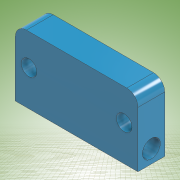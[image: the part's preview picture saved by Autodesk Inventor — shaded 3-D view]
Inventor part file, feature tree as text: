
AUTODESK INVENTOR PART (.ipt)
format: ipt  version: 2022 (Build 260153000, 153)  size: 151,040 bytes
history: native  units: mm
features: extrude x3, sketch x3, other x1, fillet x1
ambient origin geometry x8: Origin, YZ Plane, XZ Plane, XY Plane, X Axis, Y Axis, Z Axis, Center Point
bodies: Body1 (feature_tree)
feature tree (8):
  other  "Sólido1"
  extrude  "Extrusión1"  Depth=55.0mm
  fillet  "Empalme1"  Radius=20.0mm
  extrude  "Extrusión5"  Depth=5.0mm
  extrude  "Extrusión6"  Depth=10.0mm TaperAngle=0.0deg
  sketch  "Boceto1"  dims[d0=7.0mm d1=55.0mm d3=20.0mm]
  sketch  "Boceto7"  dims[d4=12.0mm d5=0.0mm d15=5.0mm]
  sketch  "Boceto8"  dims[d23=42.67mm d24=10.0mm d25=0.0mm d26=8.0mm d27=6.0mm d29=55.0mm d30=0.0mm d32=6.0mm]
